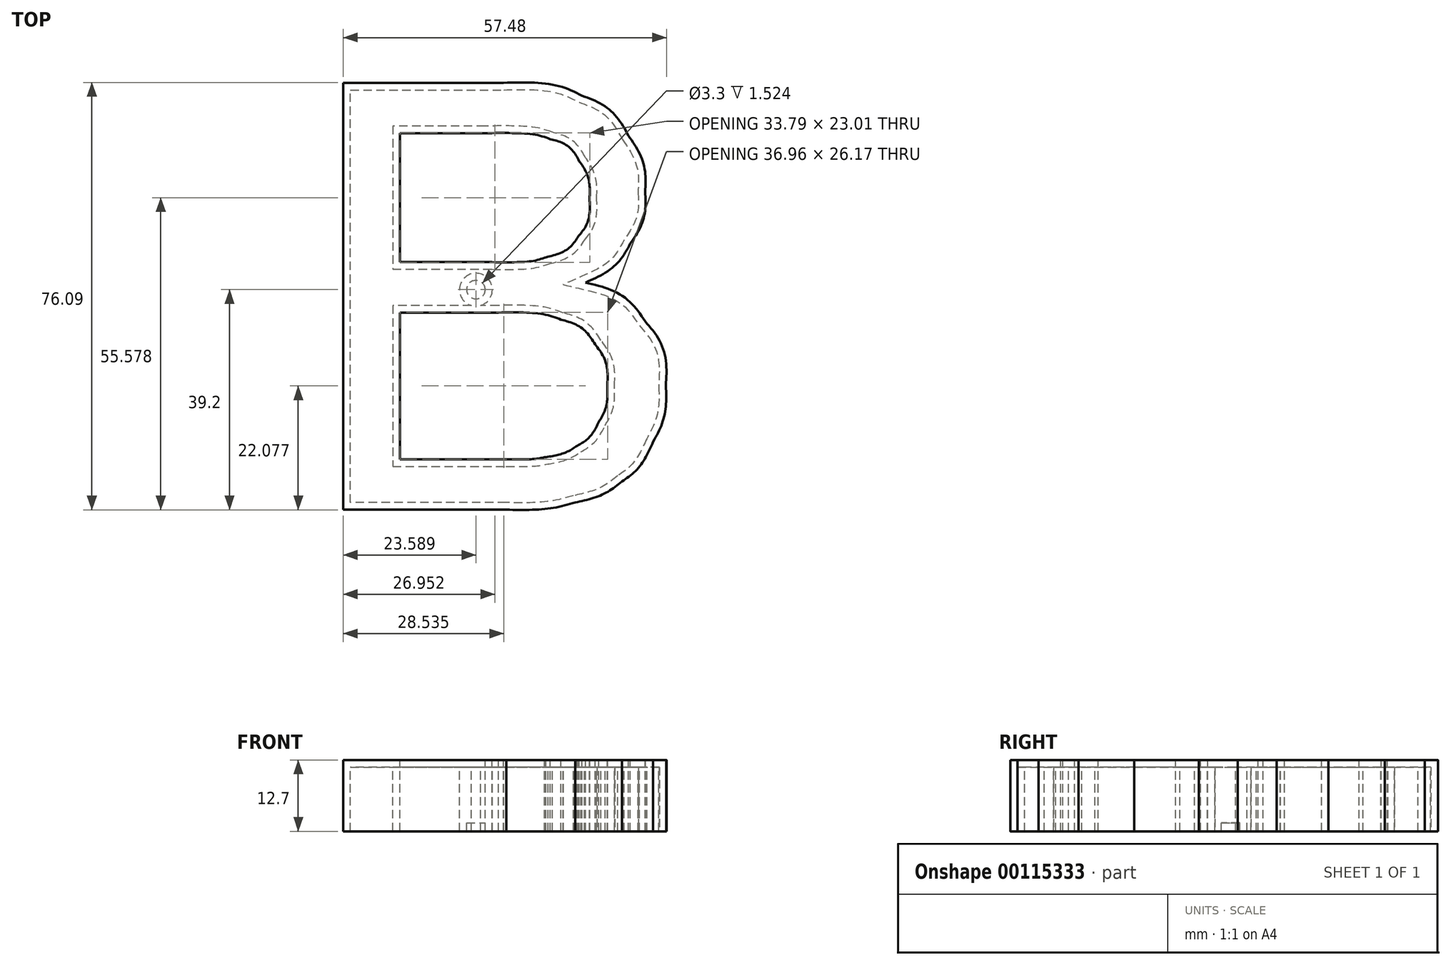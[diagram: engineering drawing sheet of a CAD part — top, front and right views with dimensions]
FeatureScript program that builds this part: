
annotation { "Feature Type Name" : "Feature", "Feature Type Description" : "" }
export const myFeature = defineFeature(function(context is Context, id is Id, definition is map)
    precondition{}
    {
        {
            var Q0;
            Q0=qCreatedBy(makeId("Top.planeOp"),FACE);
            var sketch = newSketch(context, id + "F0", { "sketchPlane" : qUnion([Q0])});
            skFitSpline(sketch, "E0", {"points": [v(-0.18, 38) * mm, v(5.62, 38) * mm, v(10.28, 37.23) * mm, v(13.79, 35.69) * mm]});
            skFitSpline(sketch, "E1", {"points": [v(13.79, 35.69) * mm, v(17.3, 34.15) * mm, v(20.04, 31.78) * mm, v(22.03, 28.59) * mm]});
            skFitSpline(sketch, "E2", {"points": [v(22.03, 28.59) * mm, v(24.02, 25.4) * mm, v(25.01, 22.05) * mm, v(25.01, 18.56) * mm]});
            skFitSpline(sketch, "E3", {"points": [v(25.01, 18.56) * mm, v(25.01, 15.3) * mm, v(24.13, 12.25) * mm, v(22.37, 9.38) * mm]});
            skFitSpline(sketch, "E4", {"points": [v(22.37, 9.38) * mm, v(20.6, 6.51) * mm, v(17.94, 4.2) * mm, v(14.38, 2.44) * mm]});
            skFitSpline(sketch, "E5", {"points": [v(14.38, 2.44) * mm, v(18.98, 1.09) * mm, v(22.51, -1.2) * mm, v(24.98, -4.46) * mm]});
            skFitSpline(sketch, "E6", {"points": [v(24.98, -4.46) * mm, v(27.46, -7.7) * mm, v(28.7, -11.54) * mm, v(28.7, -15.97) * mm]});
            skFitSpline(sketch, "E7", {"points": [v(28.7, -15.97) * mm, v(28.7, -19.52) * mm, v(27.94, -22.83) * mm, v(26.44, -25.9) * mm]});
            skFitSpline(sketch, "E8", {"points": [v(26.44, -25.9) * mm, v(24.93, -28.95) * mm, v(23.08, -31.3) * mm, v(20.86, -32.97) * mm]});
            skFitSpline(sketch, "E9", {"points": [v(20.86, -32.97) * mm, v(18.65, -34.63) * mm, v(15.88, -35.88) * mm, v(12.54, -36.73) * mm]});
            skFitSpline(sketch, "E10", {"points": [v(12.54, -36.73) * mm, v(9.2, -37.57) * mm, v(5.12, -38) * mm, v(0.29, -38) * mm]});
            skLineSegment(sketch, "E11", {"start": v(-28.7, -38) * mm, "end": v(-28.7, 38) * mm});
            skLineSegment(sketch, "E12", {"start": v(-28.7, 38) * mm, "end": v(-0.18, 38) * mm});
            skLineSegment(sketch, "E13", {"start": v(0.29, -38) * mm, "end": v(-28.7, -38) * mm});
            skFitSpline(sketch, "E14", {"points": [v(-2.2, 6.06) * mm, v(2.25, 6.06) * mm, v(5.45, 6.36) * mm, v(7.39, 6.95) * mm]});
            skFitSpline(sketch, "E15", {"points": [v(7.39, 6.95) * mm, v(9.94, 7.7) * mm, v(11.87, 8.97) * mm, v(13.17, 10.73) * mm]});
            skFitSpline(sketch, "E16", {"points": [v(13.17, 10.73) * mm, v(14.46, 12.5) * mm, v(15.1, 14.7) * mm, v(15.1, 17.36) * mm]});
            skFitSpline(sketch, "E17", {"points": [v(15.1, 17.36) * mm, v(15.1, 19.89) * mm, v(14.5, 22.1) * mm, v(13.3, 24.03) * mm]});
            skFitSpline(sketch, "E18", {"points": [v(13.3, 24.03) * mm, v(12.09, 25.94) * mm, v(10.36, 27.26) * mm, v(8.11, 27.97) * mm]});
            skFitSpline(sketch, "E19", {"points": [v(8.11, 27.97) * mm, v(5.87, 28.67) * mm, v(2.01, 29.03) * mm, v(-3.45, 29.03) * mm]});
            skLineSegment(sketch, "E20", {"start": v(-18.63, 6.06) * mm, "end": v(-2.2, 6.06) * mm});
            skLineSegment(sketch, "E21", {"start": v(-3.45, 29.03) * mm, "end": v(-18.63, 29.03) * mm});
            skLineSegment(sketch, "E22", {"start": v(-18.63, 29.03) * mm, "end": v(-18.63, 6.06) * mm});
            skFitSpline(sketch, "E23", {"points": [v(0.29, -29.03) * mm, v(3.53, -29.03) * mm, v(5.81, -28.9) * mm, v(7.13, -28.66) * mm]});
            skFitSpline(sketch, "E24", {"points": [v(7.13, -28.66) * mm, v(9.44, -28.25) * mm, v(11.38, -27.56) * mm, v(12.93, -26.6) * mm]});
            skFitSpline(sketch, "E25", {"points": [v(12.93, -26.6) * mm, v(14.49, -25.62) * mm, v(15.77, -24.22) * mm, v(16.77, -22.37) * mm]});
            skFitSpline(sketch, "E26", {"points": [v(16.77, -22.37) * mm, v(17.77, -20.52) * mm, v(18.27, -18.38) * mm, v(18.27, -15.97) * mm]});
            skFitSpline(sketch, "E27", {"points": [v(18.27, -15.97) * mm, v(18.27, -13.13) * mm, v(17.55, -10.67) * mm, v(16.1, -8.58) * mm]});
            skFitSpline(sketch, "E28", {"points": [v(16.1, -8.58) * mm, v(14.64, -6.49) * mm, v(12.63, -5.02) * mm, v(10.06, -4.17) * mm]});
            skFitSpline(sketch, "E29", {"points": [v(10.06, -4.17) * mm, v(7.48, -3.33) * mm, v(3.78, -2.9) * mm, v(-1.06, -2.9) * mm]});
            skLineSegment(sketch, "E30", {"start": v(-18.63, -29.03) * mm, "end": v(0.29, -29.03) * mm});
            skLineSegment(sketch, "E31", {"start": v(-1.06, -2.9) * mm, "end": v(-18.63, -2.9) * mm});
            skLineSegment(sketch, "E32", {"start": v(-18.63, -2.9) * mm, "end": v(-18.63, -29.03) * mm});
            skSolve(sketch);
        }
        {
            var Q0;
            Q0=makeQuery(id+"F0.imprint","IMPRINT",FACE,{"disambiguationData":[TD([[makeQuery(id+"F0.imprint","IMPRINT",EDGE,{"derivedFrom":sQuery(id+"F0.wireOp",EDGE,"E0")}),-1.0]])]});
            extrude(context, id + "F1", {"entities" : qUnion([Q0]), "oppositeDirection" : true, "depth" : 12.7 * mm});
        }
        {
            var Q0;
            Q0=makeQuery(id+"F1.opExtrude","CAP_FACE",FACE,{"disambiguationData":[OSD([sQuery(id+"F0.wireOp",EDGE,"E0"),sQuery(id+"F0.wireOp",EDGE,"E1"),sQuery(id+"F0.wireOp",EDGE,"E2"),sQuery(id+"F0.wireOp",EDGE,"E3"),sQuery(id+"F0.wireOp",EDGE,"E4"),sQuery(id+"F0.wireOp",EDGE,"E5"),sQuery(id+"F0.wireOp",EDGE,"E6"),sQuery(id+"F0.wireOp",EDGE,"E7"),sQuery(id+"F0.wireOp",EDGE,"E8"),sQuery(id+"F0.wireOp",EDGE,"E9"),sQuery(id+"F0.wireOp",EDGE,"E10"),sQuery(id+"F0.wireOp",EDGE,"E11"),sQuery(id+"F0.wireOp",EDGE,"E12"),sQuery(id+"F0.wireOp",EDGE,"E13"),sQuery(id+"F0.wireOp",EDGE,"E14"),sQuery(id+"F0.wireOp",EDGE,"E15"),sQuery(id+"F0.wireOp",EDGE,"E16"),sQuery(id+"F0.wireOp",EDGE,"E17"),sQuery(id+"F0.wireOp",EDGE,"E18"),sQuery(id+"F0.wireOp",EDGE,"E19"),sQuery(id+"F0.wireOp",EDGE,"E20"),sQuery(id+"F0.wireOp",EDGE,"E21"),sQuery(id+"F0.wireOp",EDGE,"E22"),sQuery(id+"F0.wireOp",EDGE,"E23"),sQuery(id+"F0.wireOp",EDGE,"E24"),sQuery(id+"F0.wireOp",EDGE,"E25"),sQuery(id+"F0.wireOp",EDGE,"E26"),sQuery(id+"F0.wireOp",EDGE,"E27"),sQuery(id+"F0.wireOp",EDGE,"E28"),sQuery(id+"F0.wireOp",EDGE,"E29"),sQuery(id+"F0.wireOp",EDGE,"E30"),sQuery(id+"F0.wireOp",EDGE,"E31"),sQuery(id+"F0.wireOp",EDGE,"E32")])],"isStart":false});
            shell(context, id + "F2", {"entities" : qUnion([Q0]), "thickness" : 1.27 * mm});
        }
        {
            var Q0;
            {var subQ0=sQuery(id+"F0.wireOp",EDGE,"E32");var subQ1=sQuery(id+"F0.wireOp",EDGE,"E31");var subQ2=sQuery(id+"F0.wireOp",EDGE,"E30");var subQ3=sQuery(id+"F0.wireOp",EDGE,"E29");var subQ4=sQuery(id+"F0.wireOp",EDGE,"E28");var subQ5=sQuery(id+"F0.wireOp",EDGE,"E27");var subQ6=sQuery(id+"F0.wireOp",EDGE,"E26");var subQ7=sQuery(id+"F0.wireOp",EDGE,"E25");var subQ8=sQuery(id+"F0.wireOp",EDGE,"E24");var subQ9=sQuery(id+"F0.wireOp",EDGE,"E23");var subQ10=sQuery(id+"F0.wireOp",EDGE,"E22");var subQ11=sQuery(id+"F0.wireOp",EDGE,"E21");var subQ12=sQuery(id+"F0.wireOp",EDGE,"E20");var subQ13=sQuery(id+"F0.wireOp",EDGE,"E19");var subQ14=sQuery(id+"F0.wireOp",EDGE,"E18");var subQ15=sQuery(id+"F0.wireOp",EDGE,"E17");var subQ16=sQuery(id+"F0.wireOp",EDGE,"E16");var subQ17=sQuery(id+"F0.wireOp",EDGE,"E15");var subQ18=sQuery(id+"F0.wireOp",EDGE,"E14");var subQ19=sQuery(id+"F0.wireOp",EDGE,"E13");var subQ20=sQuery(id+"F0.wireOp",EDGE,"E12");var subQ21=sQuery(id+"F0.wireOp",EDGE,"E11");var subQ22=sQuery(id+"F0.wireOp",EDGE,"E10");var subQ23=sQuery(id+"F0.wireOp",EDGE,"E9");var subQ24=sQuery(id+"F0.wireOp",EDGE,"E8");var subQ25=sQuery(id+"F0.wireOp",EDGE,"E7");var subQ26=sQuery(id+"F0.wireOp",EDGE,"E6");var subQ27=sQuery(id+"F0.wireOp",EDGE,"E5");var subQ28=sQuery(id+"F0.wireOp",EDGE,"E4");var subQ29=sQuery(id+"F0.wireOp",EDGE,"E3");var subQ30=sQuery(id+"F0.wireOp",EDGE,"E2");var subQ31=sQuery(id+"F0.wireOp",EDGE,"E1");var subQ32=sQuery(id+"F0.wireOp",EDGE,"E0");Q0=makeQuery(id+"F2.opShell","OFFSET_FACE",FACE,{"disambiguationData":[OSD([subQ32,subQ31,subQ30,subQ29,subQ28,subQ27,subQ26,subQ25,subQ24,subQ23,subQ22,subQ21,subQ20,subQ19,subQ18,subQ17,subQ16,subQ15,subQ14,subQ13,subQ12,subQ11,subQ10,subQ9,subQ8,subQ7,subQ6,subQ5,subQ4,subQ3,subQ2,subQ1,subQ0]),TDD([makeQuery(id+"F1.opExtrude","CAP_FACE",FACE,{"disambiguationData":[OSD([subQ32,subQ31,subQ30,subQ29,subQ28,subQ27,subQ26,subQ25,subQ24,subQ23,subQ22,subQ21,subQ20,subQ19,subQ18,subQ17,subQ16,subQ15,subQ14,subQ13,subQ12,subQ11,subQ10,subQ9,subQ8,subQ7,subQ6,subQ5,subQ4,subQ3,subQ2,subQ1,subQ0])],"isStart":true})])]});}
            var sketch = newSketch(context, id + "F3", { "sketchPlane" : qUnion([Q0])});
            skCircle(sketch, "E33", {"center": v(-5.1, -1.17) * mm, "radius": 1.65 * mm});
            skCircle(sketch, "E34.0", {"center": v(-5.1, -1.17) * mm, "radius": 2.92 * mm});
            skSolve(sketch);
        }
        {
            var Q0;
            Q0=makeQuery(id+"F3.imprint","IMPRINT",FACE,{"disambiguationData":[TD([[makeQuery(id+"F3.imprint","IMPRINT",EDGE,{"derivedFrom":sQuery(id+"F3.wireOp",EDGE,"E33")}),-1.0]])]});
            extrude(context, id + "F4", {"entities" : qUnion([Q0]), "operationType" : NewBodyOperationType.ADD, "depth" : 11.43 * mm});
        }
        {
            var Q0;
            {var subQ0=sQuery(id+"F0.wireOp",EDGE,"E32");var subQ1=sQuery(id+"F0.wireOp",EDGE,"E31");var subQ2=sQuery(id+"F0.wireOp",EDGE,"E30");var subQ3=sQuery(id+"F0.wireOp",EDGE,"E29");var subQ4=sQuery(id+"F0.wireOp",EDGE,"E28");var subQ5=sQuery(id+"F0.wireOp",EDGE,"E27");var subQ6=sQuery(id+"F0.wireOp",EDGE,"E26");var subQ7=sQuery(id+"F0.wireOp",EDGE,"E25");var subQ8=sQuery(id+"F0.wireOp",EDGE,"E24");var subQ9=sQuery(id+"F0.wireOp",EDGE,"E23");var subQ10=sQuery(id+"F0.wireOp",EDGE,"E22");var subQ11=sQuery(id+"F0.wireOp",EDGE,"E21");var subQ12=sQuery(id+"F0.wireOp",EDGE,"E20");var subQ13=sQuery(id+"F0.wireOp",EDGE,"E19");var subQ14=sQuery(id+"F0.wireOp",EDGE,"E18");var subQ15=sQuery(id+"F0.wireOp",EDGE,"E17");var subQ16=sQuery(id+"F0.wireOp",EDGE,"E16");var subQ17=sQuery(id+"F0.wireOp",EDGE,"E15");var subQ18=sQuery(id+"F0.wireOp",EDGE,"E14");var subQ19=sQuery(id+"F0.wireOp",EDGE,"E13");var subQ20=sQuery(id+"F0.wireOp",EDGE,"E12");var subQ21=sQuery(id+"F0.wireOp",EDGE,"E11");var subQ22=sQuery(id+"F0.wireOp",EDGE,"E10");var subQ23=sQuery(id+"F0.wireOp",EDGE,"E9");var subQ24=sQuery(id+"F0.wireOp",EDGE,"E8");var subQ25=sQuery(id+"F0.wireOp",EDGE,"E7");var subQ26=sQuery(id+"F0.wireOp",EDGE,"E6");var subQ27=sQuery(id+"F0.wireOp",EDGE,"E5");var subQ28=sQuery(id+"F0.wireOp",EDGE,"E4");var subQ29=sQuery(id+"F0.wireOp",EDGE,"E3");var subQ30=sQuery(id+"F0.wireOp",EDGE,"E2");var subQ31=sQuery(id+"F0.wireOp",EDGE,"E1");var subQ32=sQuery(id+"F0.wireOp",EDGE,"E0");Q0=makeQuery(id+"F4.boolean.opBoolean","SPLIT",FACE,{"disambiguationData":[TD([makeQuery(id+"F4.opExtrude","SWEPT_FACE",FACE,{"disambiguationData":[OSD([sQuery(id+"F3.wireOp",EDGE,"E33")])]})])],"derivedFrom":makeQuery(id+"F2.opShell","OFFSET_FACE",FACE,{"disambiguationData":[OSD([subQ32,subQ31,subQ30,subQ29,subQ28,subQ27,subQ26,subQ25,subQ24,subQ23,subQ22,subQ21,subQ20,subQ19,subQ18,subQ17,subQ16,subQ15,subQ14,subQ13,subQ12,subQ11,subQ10,subQ9,subQ8,subQ7,subQ6,subQ5,subQ4,subQ3,subQ2,subQ1,subQ0]),TDD([makeQuery(id+"F1.opExtrude","CAP_FACE",FACE,{"disambiguationData":[OSD([subQ32,subQ31,subQ30,subQ29,subQ28,subQ27,subQ26,subQ25,subQ24,subQ23,subQ22,subQ21,subQ20,subQ19,subQ18,subQ17,subQ16,subQ15,subQ14,subQ13,subQ12,subQ11,subQ10,subQ9,subQ8,subQ7,subQ6,subQ5,subQ4,subQ3,subQ2,subQ1,subQ0])],"isStart":true})])]})});}
            extrude(context, id + "F5", {"entities" : qUnion([Q0]), "operationType" : NewBodyOperationType.ADD, "depth" : 9.9 * mm});
        }
    });
